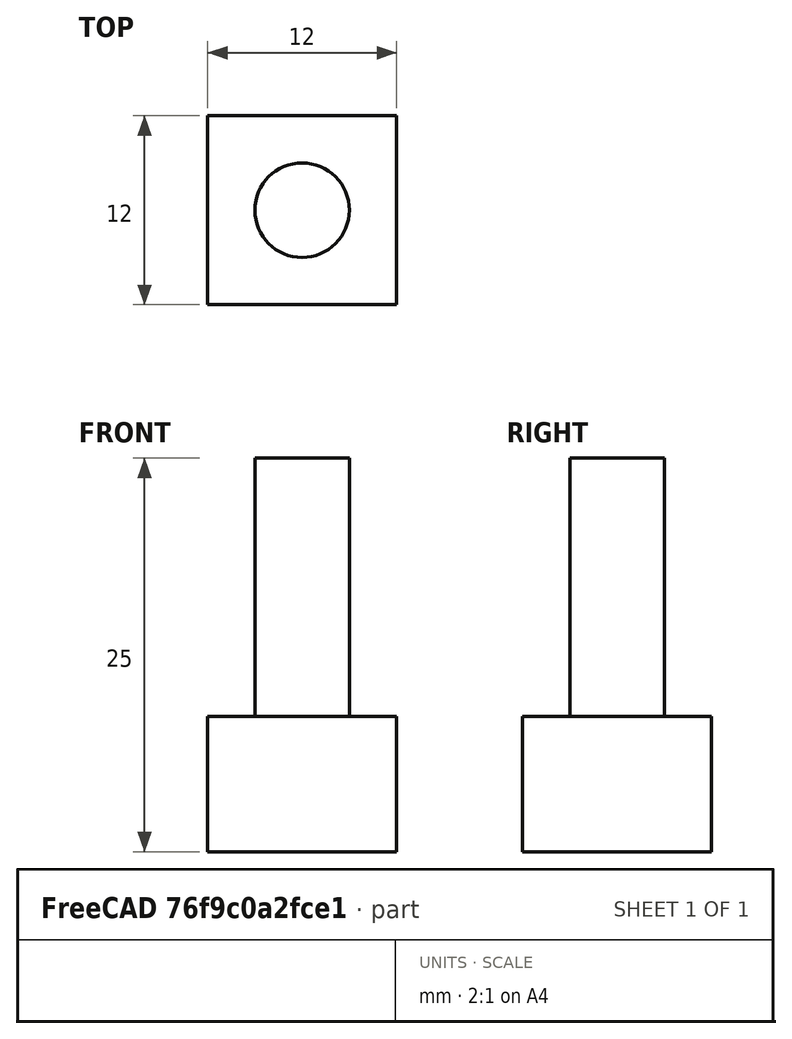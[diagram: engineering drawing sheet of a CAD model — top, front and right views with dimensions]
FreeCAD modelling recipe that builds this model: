
FCSTD DOCUMENT  (FreeCAD 0.19R24276 (Git))
Label: EC11
License: All rights reserved
LicenseURL: http://en.wikipedia.org/wiki/All_rights_reserved
objects: PartDesign::AdditiveBox×1, PartDesign::AdditiveCylinder×1, PartDesign::Body×1
note: 5 computed .brp shape members not serialized (recipe doc carries the construction recipe); baked Part::Feature solids carry a one-line shape summary decoded from their .brp

FEATURE [PartDesign::AdditiveBox] Box012
  AttacherType = Attacher::AttachEngine3D
  AttachmentOffset = pos=(-6,-6,0) rot=(0,0,1;0rad)
  Height = 8.6
  Length = 12
  MapMode = 5
  Placement = pos=(-6,-6,0) rot=(0,0,1;0rad)
  Refine = true
  Support = -> [XY_Plane029]
  Width = 12
FEATURE [PartDesign::AdditiveCylinder] Cylinder003
  Angle = 360
  AttacherType = Attacher::AttachEngine3D
  BaseFeature = -> Box012
  Height = 25
  Radius = 3
  Refine = true
FEATURE [PartDesign::Body] Body026003  label="EC11_Encoder"
  Group = -> [Box012,Cylinder003]
  Origin = -> Origin029
  Tip = -> Cylinder003
